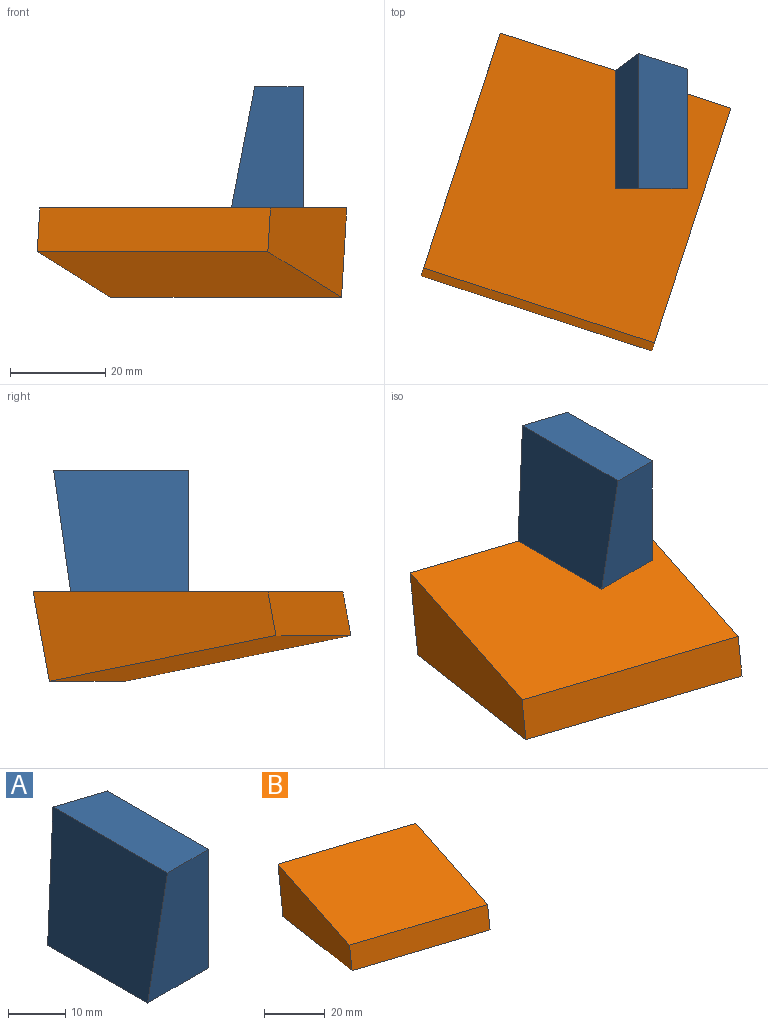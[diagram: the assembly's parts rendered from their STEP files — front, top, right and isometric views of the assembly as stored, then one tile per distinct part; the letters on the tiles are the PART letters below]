
ASSEMBLY  parts=2 mates=1
PART A: 6 faces, bbox 15x28.3x25.4 mm
  f0: plane 24.75x15.01mm, normal (0,0,-1), area 335mm2, adj f1,f3,f4,f5
  f1: plane 25.4x25mm, normal (1,0,0), area 569.9mm2, adj f0,f2,f4,f5
  f2: plane 28.29x10.14mm, normal (0,0,1), area 270.1mm2, adj f1,f3,f4,f5
  f3: plane 28.29x25.4mm, normal (-0.98,0,0.19), area 686mm2, adj f0,f2,f4,f5
  f4: plane 25.4x15.01mm, normal (0,-1,0), area 319.4mm2, adj f0,f1,f2,f3
  f5: plane 25.4x15.01mm, normal (0.3,0.93,-0.19), area 342mm2, adj f0,f1,f2,f3
PART B: 6 faces, bbox 64.8x66.6x18.7 mm
  f0: plane 49.42x19.12mm, normal (0.3,0.93,-0.19), area 967.7mm2, adj f1,f3,f4,f5
  f1: plane 64.9x64.3mm, normal (0,0,1), area 2627.8mm2, adj f0,f2,f4,f5
  f2: plane 48.86x17.37mm, normal (-0.3,-0.93,0.19), area 472.1mm2, adj f1,f3,f4,f5
  f3: plane 63.73x63.14mm, normal (-0.06,-0.18,-0.98), area 2580.6mm2, adj f0,f2,f4,f5
  f4: plane 50.86x18.71mm, normal (0.95,-0.31,0), area 719.9mm2, adj f0,f1,f2,f3
  f5: plane 50.86x18.71mm, normal (-0.95,0.31,0), area 719.9mm2, adj f0,f1,f2,f3
PLACE A at identity
PLACE B at identity fixed
MATE fastened A.f0 <-> B.f1  axis (0,0,-1) through (-4.85,5.7,0)mm
